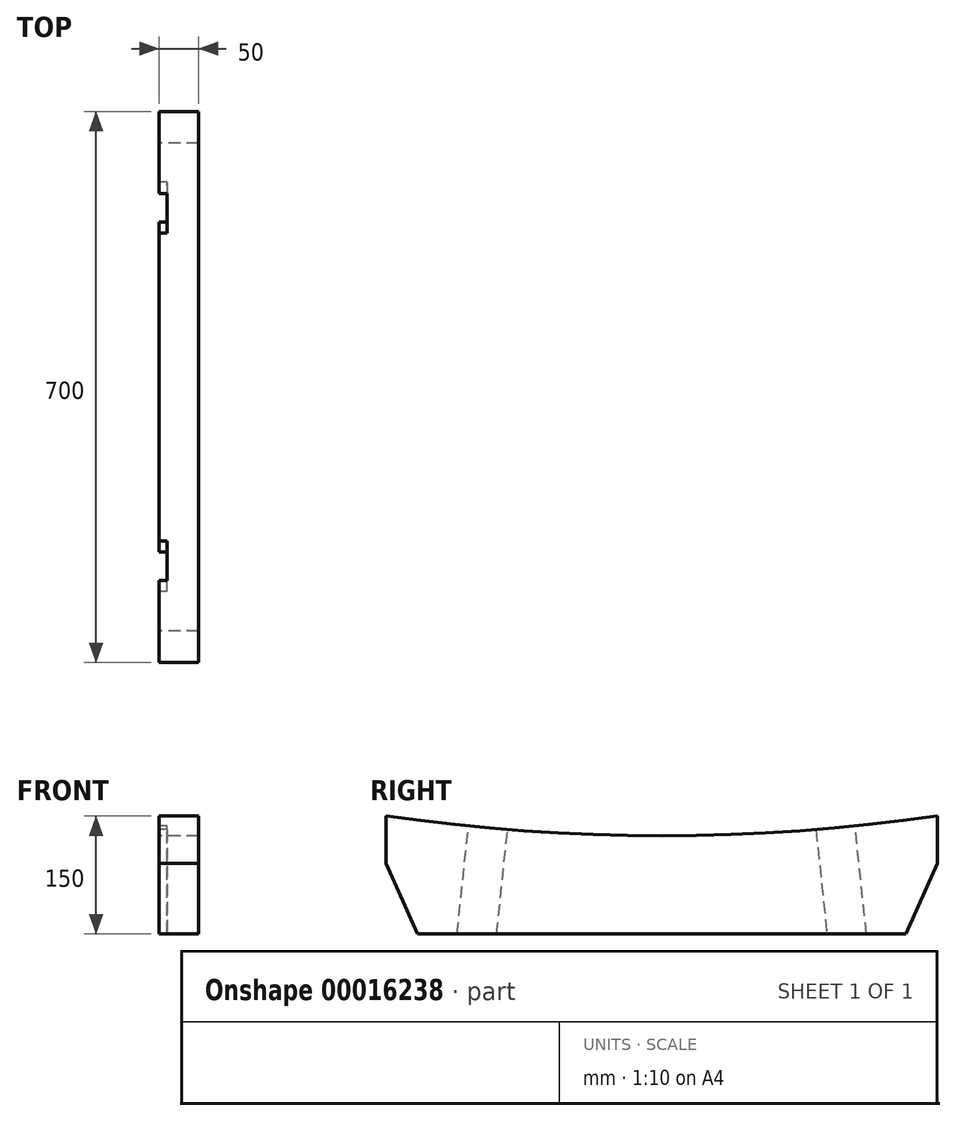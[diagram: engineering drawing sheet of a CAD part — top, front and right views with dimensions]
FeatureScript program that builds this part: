
annotation { "Feature Type Name" : "Feature", "Feature Type Description" : "" }
export const myFeature = defineFeature(function(context is Context, id is Id, definition is map)
    precondition{}
    {
        {
            var Q0;
            Q0=qCreatedBy(makeId("Right.planeOp"),FACE);
            var sketch = newSketch(context, id + "F0", { "sketchPlane" : qUnion([Q0])});
            skLineSegment(sketch, "E0.top", {"start": v(-324.18, -180.95) * mm, "end": v(295.82, -180.95) * mm});
            skLineSegment(sketch, "E0.left", {"start": v(-364.18, -30.95) * mm, "end": v(-364.18, -90.95) * mm});
            skLineSegment(sketch, "E0.right", {"start": v(335.82, -30.95) * mm, "end": v(335.82, -90.95) * mm});
            skArc(sketch, "E1", {"start": v(-364.18, -30.95) * mm, "mid": v(-14.18, -55.95) * mm, "end": v(335.82, -30.95) * mm});
            skLineSegment(sketch, "E2", {"start": v(295.82, -180.95) * mm, "end": v(335.82, -90.95) * mm});
            skLineSegment(sketch, "E3", {"start": v(-364.18, -90.95) * mm, "end": v(-324.18, -180.95) * mm});
            skSolve(sketch);
        }
        {
            var Q0;
            Q0=makeQuery(id+"F0.imprint","IMPRINT",FACE,{"disambiguationData":[TD([[makeQuery(id+"F0.imprint","IMPRINT",EDGE,{"derivedFrom":sQuery(id+"F0.wireOp",EDGE,"E0.top")}),1.0]])]});
            extrude(context, id + "F1", {"entities" : qUnion([Q0]), "depth" : 50 * mm});
        }
        {
            var Q0;
            Q0=makeQuery(id+"F1.opExtrude","CAP_FACE",FACE,{"disambiguationData":[OSD([sQuery(id+"F0.wireOp",EDGE,"E0.top"),sQuery(id+"F0.wireOp",EDGE,"E0.left"),sQuery(id+"F0.wireOp",EDGE,"E0.right"),sQuery(id+"F0.wireOp",EDGE,"E1"),sQuery(id+"F0.wireOp",EDGE,"E2"),sQuery(id+"F0.wireOp",EDGE,"E3")])],"isStart":true});
            var sketch = newSketch(context, id + "F2", { "sketchPlane" : qUnion([Q0])});
            skLineSegment(sketch, "E4", {"start": v(324.18, -180.95) * mm, "end": v(274.18, -180.95) * mm});
            skLineSegment(sketch, "E5", {"start": v(274.18, -180.95) * mm, "end": v(259.67, -42.93) * mm});
            skLineSegment(sketch, "E6", {"start": v(274.18, -180.95) * mm, "end": v(223.9, -180.95) * mm});
            skLineSegment(sketch, "E7", {"start": v(223.9, -180.95) * mm, "end": v(209.95, -48.16) * mm});
            skLineSegment(sketch, "E8", {"start": v(-295.82, -180.95) * mm, "end": v(-245.82, -180.95) * mm});
            skLineSegment(sketch, "E9", {"start": v(-245.82, -180.95) * mm, "end": v(-231.31, -42.93) * mm});
            skLineSegment(sketch, "E10", {"start": v(-231.31, -42.93) * mm, "end": v(-181.59, -48.16) * mm});
            skLineSegment(sketch, "E11", {"start": v(-181.59, -48.16) * mm, "end": v(-195.54, -180.95) * mm});
            skLineSegment(sketch, "E12", {"start": v(-195.54, -180.95) * mm, "end": v(-245.82, -180.95) * mm});
            skLineSegment(sketch, "E13", {"start": v(-245.82, -180.95) * mm, "end": v(-295.82, -180.95) * mm});
            skLineSegment(sketch, "E14", {"start": v(209.95, -48.16) * mm, "end": v(259.67, -42.93) * mm});
            skSolve(sketch);
        }
        {
            var Q0;
            Q0 = qSketchRegion(id + "F2", true);
            extrude(context, id + "F3", {"entities" : qUnion([Q0]), "operationType" : NewBodyOperationType.REMOVE, "oppositeDirection" : true, "depth" : 10 * mm});
        }
    });
